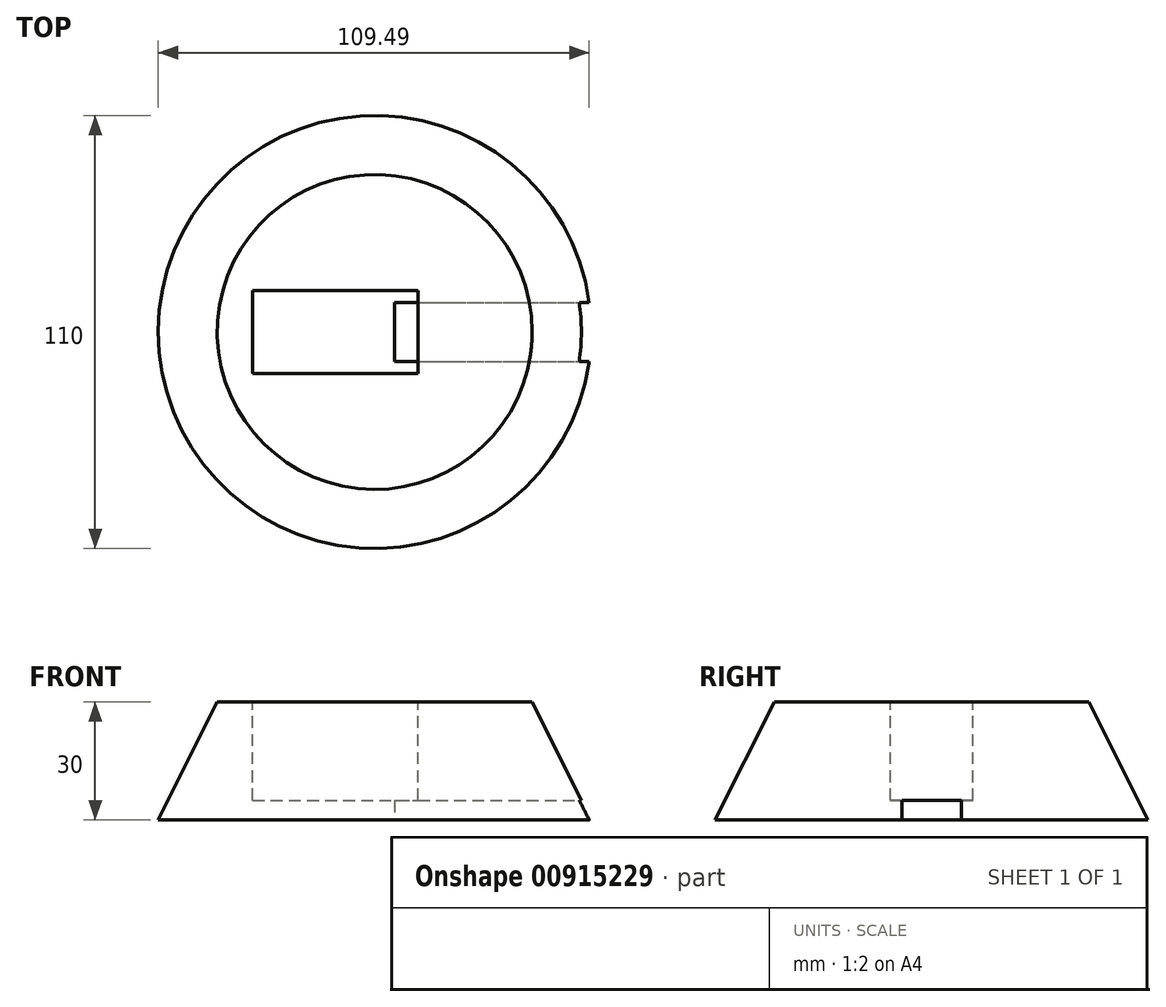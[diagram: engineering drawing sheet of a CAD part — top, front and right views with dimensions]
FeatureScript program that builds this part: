
annotation { "Feature Type Name" : "Feature", "Feature Type Description" : "" }
export const myFeature = defineFeature(function(context is Context, id is Id, definition is map)
    precondition{}
    {
        {
            var Q0;
            Q0=qCreatedBy(makeId("Top.planeOp"),FACE);
            var sketch = newSketch(context, id + "F0", { "sketchPlane" : qUnion([Q0])});
            skCircle(sketch, "E0", {"center": v(0, 0) * mm, "radius": 40 * mm});
            skSolve(sketch);
        }
        {
            var Q0;
            Q0=qCreatedBy(makeId("Top.planeOp"),FACE);
            cPlane(context, id + "F1", {"entities" : qUnion([Q0]), "cplaneType" : CPlaneType.OFFSET, "offset" : 30 * mm, "oppositeDirection" : true, "width" : 150 * mm, "height" : 150 * mm});
        }
        {
            var Q0;
            Q0=qCreatedBy(id+"F1.planeOp",FACE);
            var sketch = newSketch(context, id + "F2", { "sketchPlane" : qUnion([Q0])});
            skCircle(sketch, "E1", {"center": v(0, 0) * mm, "radius": 55 * mm});
            skSolve(sketch);
        }
        {
            var Q0;
            Q0=qCreatedBy(makeId("Top.planeOp"),FACE);
            var sketch = newSketch(context, id + "F3", { "sketchPlane" : qUnion([Q0])});
            skLineSegment(sketch, "E2.top", {"start": v(0, 10.5) * mm, "end": v(11, 10.5) * mm});
            skLineSegment(sketch, "E2.right", {"start": v(11, 0) * mm, "end": v(11, 10.5) * mm});
            skLineSegment(sketch, "E3.bottom", {"start": v(11, 10.5) * mm, "end": v(-31, 10.5) * mm});
            skLineSegment(sketch, "E3.top", {"start": v(11, -10.5) * mm, "end": v(-31, -10.5) * mm});
            skLineSegment(sketch, "E3.left", {"start": v(11, 10.5) * mm, "end": v(11, -10.5) * mm});
            skLineSegment(sketch, "E3.right", {"start": v(-31, 10.5) * mm, "end": v(-31, -10.5) * mm});
            skLineSegment(sketch, "E4", {"start": v(0, 0) * mm, "end": v(0, 10.5) * mm});
            skLineSegment(sketch, "E5", {"start": v(0, 0) * mm, "end": v(11, 0) * mm});
            skSolve(sketch);
        }
        {
            var Q0;
            Q0=makeQuery(id+"F0.imprint","IMPRINT",FACE,{"disambiguationData":[TD([[makeQuery(id+"F0.imprint","IMPRINT",EDGE,{"derivedFrom":sQuery(id+"F0.wireOp",EDGE,"E0")}),1.0]])]});
            var Q1;
            Q1=makeQuery(id+"F2.imprint","IMPRINT",FACE,{"disambiguationData":[TD([[makeQuery(id+"F2.imprint","IMPRINT",EDGE,{"derivedFrom":sQuery(id+"F2.wireOp",EDGE,"E1")}),1.0]])]});
            loft(context, id + "F4", {"sheetProfilesArray" : [{ "sheetProfileEntities" : qUnion([Q0]) }, { "sheetProfileEntities" : qUnion([Q1]) }]});
        }
        {
            var Q0;
            Q0 = qSketchRegion(id + "F3", true);
            extrude(context, id + "F5", {"entities" : qUnion([Q0]), "operationType" : NewBodyOperationType.REMOVE, "oppositeDirection" : true, "depth" : 15 * mm, "offsetDistance" : 25 * mm});
        }
        {
            var Q0;
            Q0=makeQuery(id+"F5.boolean.opBoolean","COPY",FACE,{"derivedFrom":makeQuery(id+"F5.opExtrude","CAP_FACE",FACE,{"disambiguationData":[OSD([sQuery(id+"F3.wireOp",EDGE,"E3.bottom"),sQuery(id+"F3.wireOp",EDGE,"E3.top"),sQuery(id+"F3.wireOp",EDGE,"E3.left"),sQuery(id+"F3.wireOp",EDGE,"E3.right")])],"isStart":false})});
            var sketch = newSketch(context, id + "F6", { "sketchPlane" : qUnion([Q0])});
            skLineSegment(sketch, "E6", {"start": v(11, 0) * mm, "end": v(11, 7.5) * mm});
            skLineSegment(sketch, "E7", {"start": v(11, 7.5) * mm, "end": v(6, 7.5) * mm});
            skLineSegment(sketch, "E8", {"start": v(6, 7.5) * mm, "end": v(6, 0) * mm});
            skPoint(sketch, "E8.endSnap0", {"position": v(6, 0) * mm});
            skLineSegment(sketch, "E9", {"start": v(6, 0) * mm, "end": v(6, -7.5) * mm});
            skLineSegment(sketch, "E10", {"start": v(6, -7.5) * mm, "end": v(11, -7.5) * mm});
            skLineSegment(sketch, "E11", {"start": v(11, -7.5) * mm, "end": v(11, 0) * mm});
            skSolve(sketch);
        }
        {
            var Q0;
            Q0=makeQuery(id+"F4.opLoft","CAP_FACE",FACE,{"disambiguationData":[OSD([makeQuery(id+"F2.imprint","IMPRINT",FACE,{"disambiguationData":[TD([[makeQuery(id+"F2.imprint","IMPRINT",EDGE,{"derivedFrom":sQuery(id+"F2.wireOp",EDGE,"E1")}),1.0]])]})])],"isStart":true});
            var sketch = newSketch(context, id + "F7", { "sketchPlane" : qUnion([Q0])});
            skLineSegment(sketch, "E12.bottom", {"start": v(5, 7.5) * mm, "end": v(56.32, 7.5) * mm});
            skLineSegment(sketch, "E12.top", {"start": v(5, -7.5) * mm, "end": v(56.32, -7.5) * mm});
            skLineSegment(sketch, "E12.left", {"start": v(5, 7.5) * mm, "end": v(5, -7.5) * mm});
            skLineSegment(sketch, "E12.right", {"start": v(56.32, 7.5) * mm, "end": v(56.32, -7.5) * mm});
            skSolve(sketch);
        }
        {
            var Q0;
            Q0 = qSketchRegion(id + "F7", true);
            extrude(context, id + "F8", {"entities" : qUnion([Q0]), "operationType" : NewBodyOperationType.REMOVE, "oppositeDirection" : true, "depth" : 5 * mm, "offsetDistance" : 25 * mm});
        }
        {
            var Q0;
            Q0=makeQuery(id+"F4.opLoft","CAP_FACE",FACE,{"disambiguationData":[OSD([makeQuery(id+"F0.imprint","IMPRINT",FACE,{"disambiguationData":[TD([[makeQuery(id+"F0.imprint","IMPRINT",EDGE,{"derivedFrom":sQuery(id+"F0.wireOp",EDGE,"E0")}),1.0]])]})])],"isStart":true});
            var sketch = newSketch(context, id + "F9", { "sketchPlane" : qUnion([Q0])});
            skLineSegment(sketch, "E13", {"start": v(0, 0) * mm, "end": v(11, 0) * mm});
            skLineSegment(sketch, "E14", {"start": v(11, 0) * mm, "end": v(11, 5) * mm});
            skLineSegment(sketch, "E15", {"start": v(11, 5) * mm, "end": v(23.5, 5) * mm});
            skLineSegment(sketch, "E16", {"start": v(23.5, 5) * mm, "end": v(23.5, -5) * mm});
            skLineSegment(sketch, "E17", {"start": v(23.5, -5) * mm, "end": v(11, -5) * mm});
            skLineSegment(sketch, "E18", {"start": v(11, -5) * mm, "end": v(11, 0) * mm});
            skSolve(sketch);
        }
        {
            var Q0;
            Q0=makeQuery(id+"F9.imprint","IMPRINT",FACE,{"disambiguationData":[TD([[makeQuery(id+"F9.imprint","IMPRINT",EDGE,{"derivedFrom":sQuery(id+"F9.wireOp",EDGE,"E14")}),1.0]])]});
            extrude(context, id + "F10", {"entities" : qUnion([Q0]), "operationType" : NewBodyOperationType.REMOVE, "oppositeDirection" : true, "depth" : 25 * mm, "offsetDistance" : 25 * mm});
        }
    });
